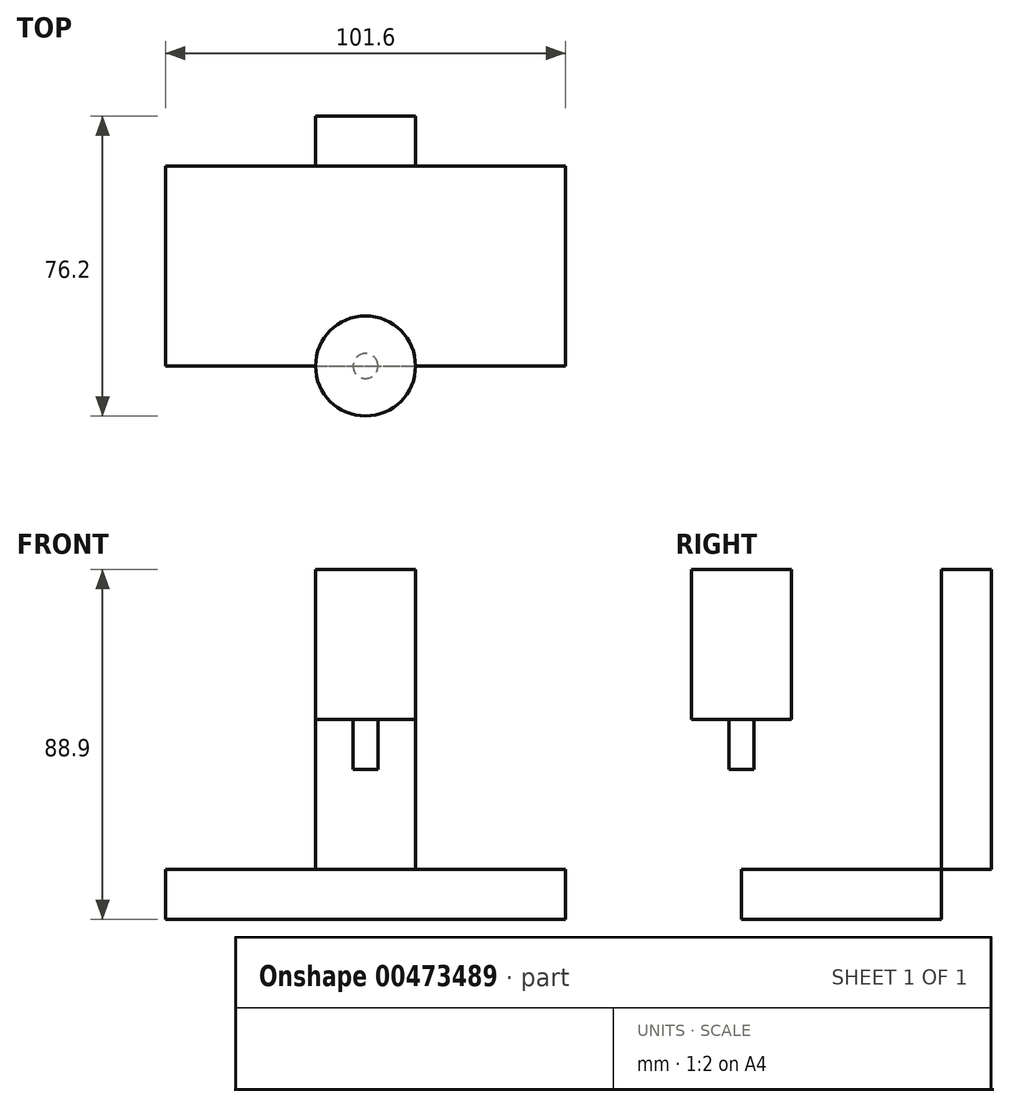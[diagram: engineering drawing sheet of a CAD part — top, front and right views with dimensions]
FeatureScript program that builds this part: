
annotation { "Feature Type Name" : "Feature", "Feature Type Description" : "" }
export const myFeature = defineFeature(function(context is Context, id is Id, definition is map)
    precondition{}
    {
        {
            var Q0;
            Q0=qCreatedBy(makeId("Top.planeOp"),FACE);
            var sketch = newSketch(context, id + "F0", { "sketchPlane" : qUnion([Q0])});
            skLineSegment(sketch, "E0.bottom", {"start": v(-50.8, 25.4) * mm, "end": v(50.8, 25.4) * mm});
            skLineSegment(sketch, "E0.top", {"start": v(-50.8, -25.4) * mm, "end": v(50.8, -25.4) * mm});
            skLineSegment(sketch, "E0.left", {"start": v(-50.8, 25.4) * mm, "end": v(-50.8, -25.4) * mm});
            skLineSegment(sketch, "E0.right", {"start": v(50.8, 25.4) * mm, "end": v(50.8, -25.4) * mm});
            skPoint(sketch, "E1", {"position": v(50.8, 0) * mm});
            skPoint(sketch, "E2", {"position": v(0, -25.4) * mm});
            skSolve(sketch);
        }
        {
            var Q0;
            Q0=makeQuery(id+"F0.imprint","IMPRINT",FACE,{"disambiguationData":[TD([[makeQuery(id+"F0.imprint","IMPRINT",EDGE,{"derivedFrom":sQuery(id+"F0.wireOp",EDGE,"E0.bottom")}),-1.0]])]});
            extrude(context, id + "F1", {"entities" : qUnion([Q0]), "depth" : 12.7 * mm});
        }
        {
            var Q0;
            Q0=makeQuery(id+"F1.opExtrude","SWEPT_FACE",FACE,{"disambiguationData":[OSD([sQuery(id+"F0.wireOp",EDGE,"E0.bottom")])]});
            var sketch = newSketch(context, id + "F2", { "sketchPlane" : qUnion([Q0])});
            skLineSegment(sketch, "E3", {"start": v(-12.7, 12.7) * mm, "end": v(-12.7, 88.9) * mm});
            skLineSegment(sketch, "E4", {"start": v(12.7, 12.7) * mm, "end": v(12.7, 88.9) * mm});
            skLineSegment(sketch, "E5", {"start": v(-12.7, 88.9) * mm, "end": v(12.7, 88.9) * mm});
            skSolve(sketch);
        }
        {
            var Q0;
            {var subQ0=sQuery(id+"F2.wireOp",EDGE,"E3");Q0=makeQuery(id+"F2.imprint","IMPRINT",FACE,{"disambiguationData":[TD([[makeQuery(id+"F2.imprint","IMPRINT",EDGE,{"derivedFrom":subQ0}),-1.0]])]});}
            extrude(context, id + "F3", {"entities" : qUnion([Q0]), "operationType" : NewBodyOperationType.ADD, "depth" : 12.7 * mm});
        }
        {
            var Q0;
            Q0=makeQuery(id+"F3.opExtrude","SWEPT_FACE",FACE,{"disambiguationData":[OSD([sQuery(id+"F2.wireOp",EDGE,"E5")])]});
            var sketch = newSketch(context, id + "F4", { "sketchPlane" : qUnion([Q0])});
            skCircle(sketch, "E6", {"center": v(0, -25.4) * mm, "radius": 12.7 * mm});
            skSolve(sketch);
        }
        {
            var Q0;
            Q0=makeQuery(id+"F4.imprint","IMPRINT",FACE,{"disambiguationData":[TD([[makeQuery(id+"F4.imprint","IMPRINT",EDGE,{"derivedFrom":sQuery(id+"F4.wireOp",EDGE,"E6")}),1.0]])]});
            extrude(context, id + "F5", {"entities" : qUnion([Q0]), "operationType" : NewBodyOperationType.ADD, "oppositeDirection" : true, "depth" : 38.1 * mm});
        }
        {
            var Q0;
            Q0=makeQuery(id+"F5.opExtrude","CAP_FACE",FACE,{"disambiguationData":[OSD([sQuery(id+"F4.wireOp",EDGE,"E6")])],"isStart":false});
            var sketch = newSketch(context, id + "F6", { "sketchPlane" : qUnion([Q0])});
            skCircle(sketch, "E7", {"center": v(0, 25.4) * mm, "radius": 3.18 * mm});
            skSolve(sketch);
        }
        {
            var Q0;
            Q0=makeQuery(id+"F6.imprint","IMPRINT",FACE,{"disambiguationData":[TD([[makeQuery(id+"F6.imprint","IMPRINT",EDGE,{"derivedFrom":sQuery(id+"F6.wireOp",EDGE,"E7")}),1.0]])]});
            extrude(context, id + "F7", {"entities" : qUnion([Q0]), "operationType" : NewBodyOperationType.ADD, "depth" : 12.7 * mm});
        }
    });
